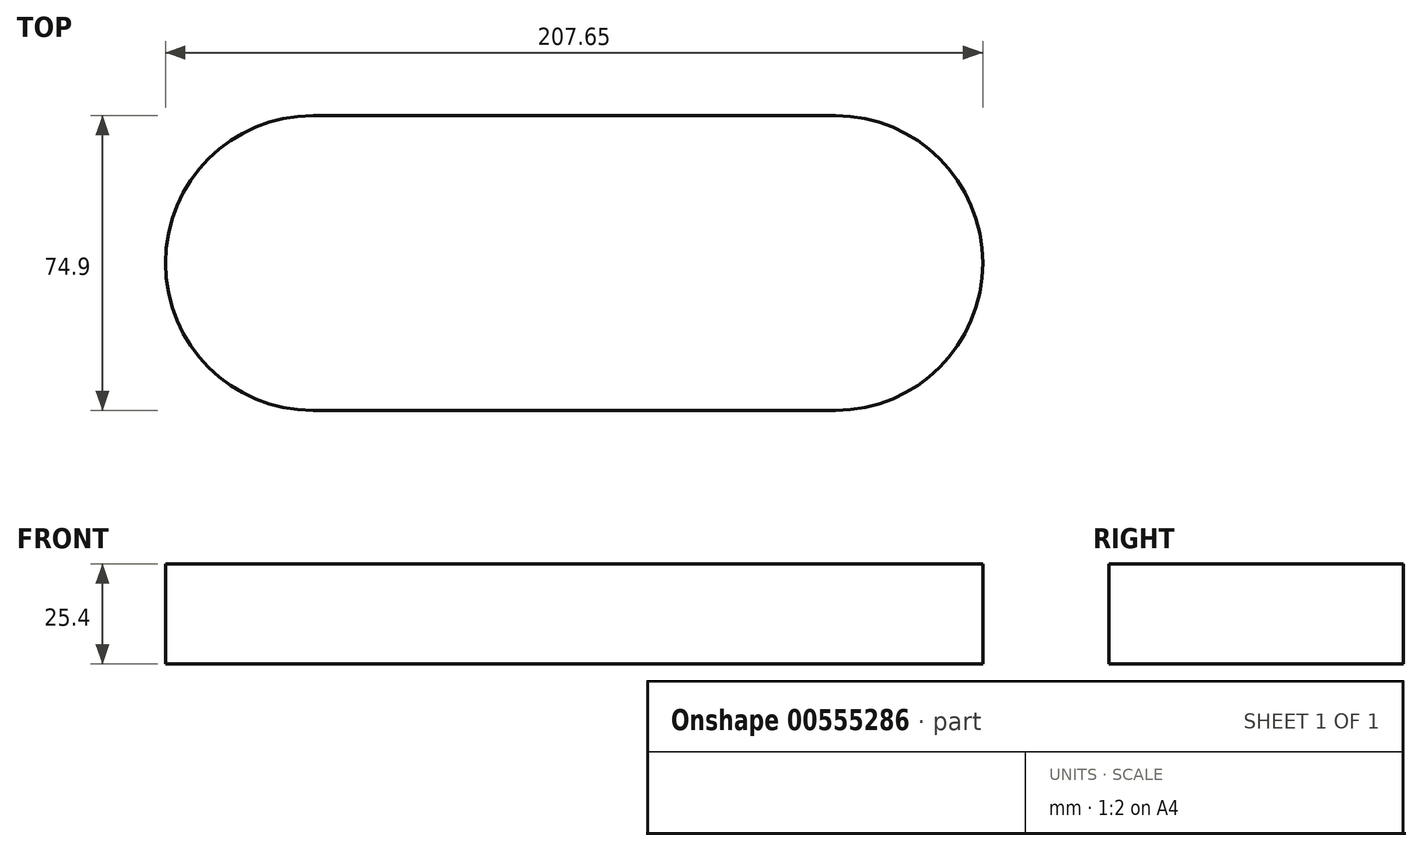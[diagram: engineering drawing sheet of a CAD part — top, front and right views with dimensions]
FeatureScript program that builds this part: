
annotation { "Feature Type Name" : "Feature", "Feature Type Description" : "" }
export const myFeature = defineFeature(function(context is Context, id is Id, definition is map)
    precondition{}
    {
        {
            var Q0;
            Q0=qCreatedBy(makeId("Top.planeOp"),FACE);
            var sketch = newSketch(context, id + "F0", { "sketchPlane" : qUnion([Q0])});
            skCircle(sketch, "E0", {"center": v(0, 0) * mm, "radius": 37.45 * mm});
            skLineSegment(sketch, "E1", {"start": v(0, -37.45) * mm, "end": v(132.75, -37.45) * mm});
            skLineSegment(sketch, "E2", {"start": v(0, 37.45) * mm, "end": v(132.75, 37.45) * mm});
            skCircle(sketch, "E3", {"center": v(132.75, 0) * mm, "radius": 37.45 * mm});
            skLineSegment(sketch, "E4", {"start": v(66.37, 37.45) * mm, "end": v(66.37, -37.45) * mm});
            skPoint(sketch, "E5", {"position": v(66.37, 0) * mm});
            skSolve(sketch);
        }
        {
            var Q0;
            Q0 = qSketchRegion(id + "F0", true);
            extrude(context, id + "F1", {"entities" : qUnion([Q0]), "depth" : 25.4 * mm, "offsetDistance" : 25.4 * mm});
        }
    });
